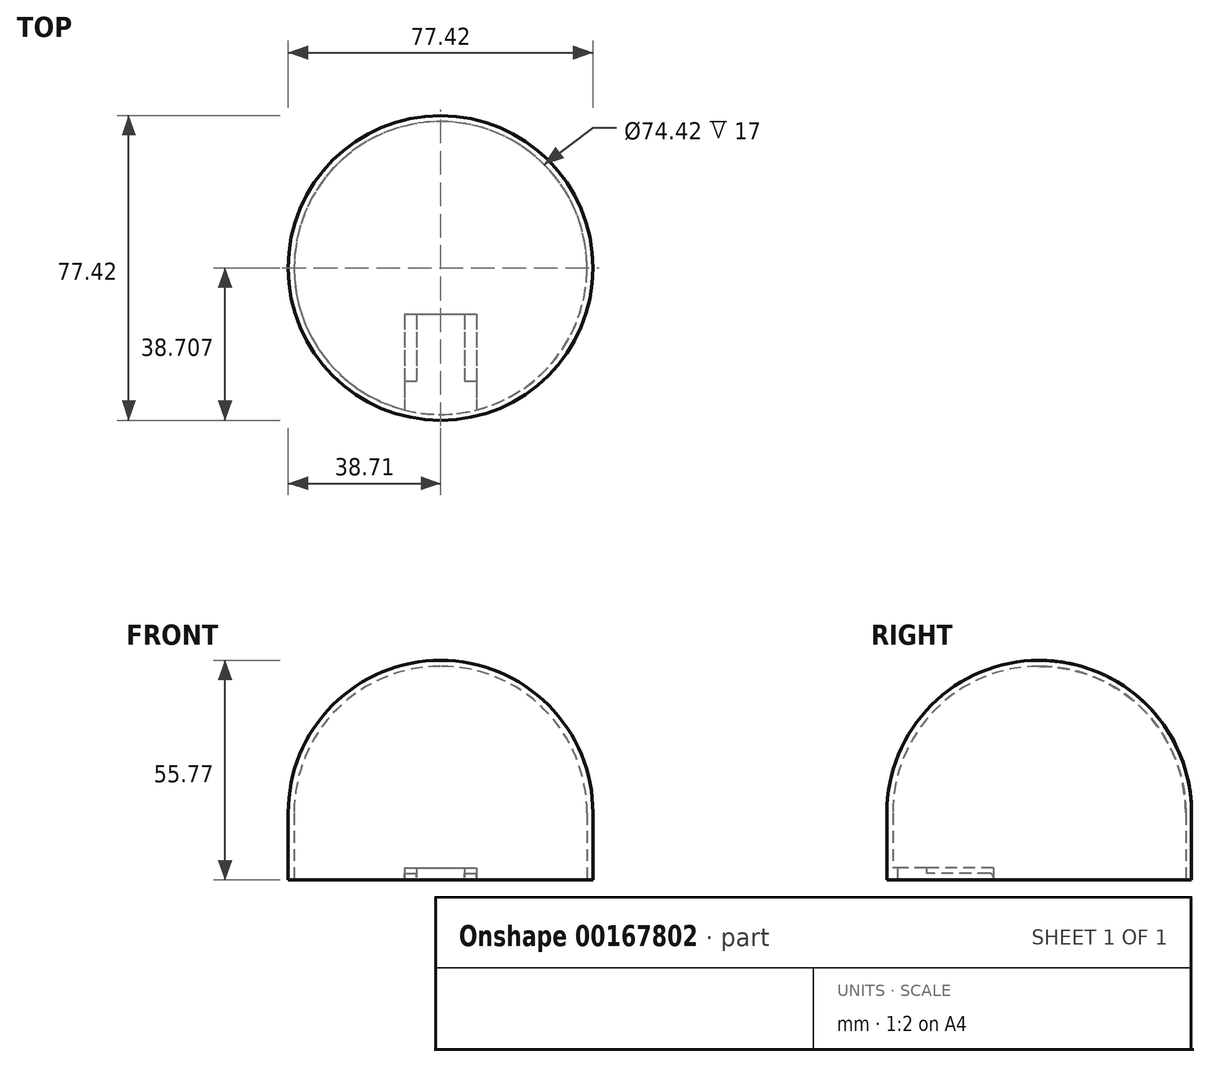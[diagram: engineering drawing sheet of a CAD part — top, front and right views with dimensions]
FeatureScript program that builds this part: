
annotation { "Feature Type Name" : "Feature", "Feature Type Description" : "" }
export const myFeature = defineFeature(function(context is Context, id is Id, definition is map)
    precondition{}
    {
        {
            var Q0;
            Q0=qCreatedBy(makeId("Top.planeOp"),FACE);
            var sketch = newSketch(context, id + "F0", { "sketchPlane" : qUnion([Q0])});
            skLineSegment(sketch, "E0.bottom", {"start": v(-9.1, 8.5) * mm, "end": v(9.1, 8.5) * mm});
            skLineSegment(sketch, "E0.top", {"start": v(-9.1, -8.5) * mm, "end": v(9.1, -8.5) * mm});
            skLineSegment(sketch, "E0.left", {"start": v(-9.1, 8.5) * mm, "end": v(-9.1, -8.5) * mm});
            skLineSegment(sketch, "E0.right", {"start": v(9.1, 8.5) * mm, "end": v(9.1, -8.5) * mm});
            skPoint(sketch, "E0.middle", {"position": v(0, 0) * mm});
            skLineSegment(sketch, "E1.bottom", {"start": v(-6.05, 8.5) * mm, "end": v(6.05, 8.5) * mm});
            skLineSegment(sketch, "E1.top", {"start": v(-6.05, -8.5) * mm, "end": v(6.05, -8.5) * mm});
            skLineSegment(sketch, "E1.left", {"start": v(-6.05, 8.5) * mm, "end": v(-6.05, -8.5) * mm});
            skLineSegment(sketch, "E1.right", {"start": v(6.05, 8.5) * mm, "end": v(6.05, -8.5) * mm});
            skLineSegment(sketch, "E2.top", {"start": v(-9.1, -16.5) * mm, "end": v(9.1, -16.5) * mm});
            skLineSegment(sketch, "E2.left", {"start": v(-9.1, -8.5) * mm, "end": v(-9.1, -16.5) * mm});
            skLineSegment(sketch, "E2.right", {"start": v(9.1, -8.5) * mm, "end": v(9.1, -16.5) * mm});
            skLineSegment(sketch, "E3", {"start": v(0, -8.5) * mm, "end": v(-26, -8.5) * mm});
            skLineSegment(sketch, "E4", {"start": v(0, -8.5) * mm, "end": v(26, -8.5) * mm});
            skLineSegment(sketch, "E5", {"start": v(0, -16.5) * mm, "end": v(0, 48.5) * mm});
            skCircle(sketch, "E6", {"center": v(0, 20.18) * mm, "radius": 38.7 * mm});
            skCircle(sketch, "E7", {"center": v(0, 20.18) * mm, "radius": 37.2 * mm});
            skSolve(sketch);
        }
        {
            var Q0;
            {var subQ0=sQuery(id+"F0.wireOp",EDGE,"E0.left");Q0=makeQuery(id+"F0.imprint","IMPRINT",FACE,{"disambiguationData":[TD([[makeQuery(id+"F0.imprint","IMPRINT",EDGE,{"derivedFrom":subQ0}),1.0]])]});}
            var Q1;
            {var subQ0=sQuery(id+"F0.wireOp",EDGE,"E0.right");Q1=makeQuery(id+"F0.imprint","IMPRINT",FACE,{"disambiguationData":[TD([[makeQuery(id+"F0.imprint","IMPRINT",EDGE,{"derivedFrom":subQ0}),-1.0]])]});}
            extrude(context, id + "F1", {"entities" : qUnion([Q0, Q1]), "depth" : 1.7 * mm});
        }
        {
            var Q0;
            {var subQ0=sQuery(id+"F0.wireOp",EDGE,"E1.left");Q0=makeQuery(id+"F0.imprint","IMPRINT",FACE,{"disambiguationData":[TD([[makeQuery(id+"F0.imprint","IMPRINT",EDGE,{"derivedFrom":subQ0}),1.0]])]});}
            var Q1;
            {var subQ0=sQuery(id+"F0.wireOp",EDGE,"E1.right");Q1=makeQuery(id+"F0.imprint","IMPRINT",FACE,{"disambiguationData":[TD([[makeQuery(id+"F0.imprint","IMPRINT",EDGE,{"derivedFrom":subQ0}),-1.0]])]});}
            var Q2;
            {var subQ4=sQuery(id+"F0.wireOp",EDGE,"E5");var subQ6=sQuery(id+"F0.wireOp",EDGE,"E2.top");var subQ7=makeQuery(id+"F0.imprint","INTERSECT",VERTEX,{"derivedFrom":[subQ6,subQ4]});Q2=makeQuery(id+"F0.imprint","IMPRINT",FACE,{"disambiguationData":[TD([[makeQuery(id+"F0.imprint","IMPRINT",EDGE,{"disambiguationData":[TD([[subQ7,1.0]])],"derivedFrom":subQ6}),1.0]])]});}
            var Q3;
            {var subQ4=sQuery(id+"F0.wireOp",EDGE,"E5");var subQ8=sQuery(id+"F0.wireOp",EDGE,"E2.top");var subQ9=makeQuery(id+"F0.imprint","INTERSECT",VERTEX,{"derivedFrom":[subQ8,subQ4]});Q3=makeQuery(id+"F0.imprint","IMPRINT",FACE,{"disambiguationData":[TD([[makeQuery(id+"F0.imprint","IMPRINT",EDGE,{"disambiguationData":[TD([[subQ9,-1.0]])],"derivedFrom":subQ8}),1.0]])]});}
            var Q4;
            {var subQ0=sQuery(id+"F0.wireOp",EDGE,"E2.top");var subQ1=makeQuery(id+"F0.imprint","INTERSECT",VERTEX,{"derivedFrom":[subQ0,sQuery(id+"F0.wireOp",EDGE,"E5")]});Q4=makeQuery(id+"F0.imprint","IMPRINT",FACE,{"disambiguationData":[TD([[makeQuery(id+"F0.imprint","IMPRINT",EDGE,{"disambiguationData":[TD([[subQ1,1.0]])],"derivedFrom":subQ0}),-1.0]])]});}
            var Q5;
            {var subQ0=sQuery(id+"F0.wireOp",EDGE,"E2.left");var subQ1=sQuery(id+"F0.wireOp",EDGE,"E2.top");var subQ2=makeQuery(id+"F0.imprint","INTERSECT",VERTEX,{"derivedFrom":[subQ1,subQ0]});Q5=makeQuery(id+"F0.imprint","IMPRINT",FACE,{"disambiguationData":[TD([[makeQuery(id+"F0.imprint","IMPRINT",EDGE,{"disambiguationData":[TD([[subQ2,-1.0]])],"derivedFrom":subQ1}),1.0]])]});}
            var Q6;
            {var subQ0=sQuery(id+"F0.wireOp",EDGE,"E2.right");var subQ1=sQuery(id+"F0.wireOp",EDGE,"E2.top");var subQ2=makeQuery(id+"F0.imprint","INTERSECT",VERTEX,{"derivedFrom":[subQ1,subQ0]});Q6=makeQuery(id+"F0.imprint","IMPRINT",FACE,{"disambiguationData":[TD([[makeQuery(id+"F0.imprint","IMPRINT",EDGE,{"disambiguationData":[TD([[subQ2,1.0]])],"derivedFrom":subQ1}),1.0]])]});}
            extrude(context, id + "F2", {"entities" : qUnion([Q0, Q1, Q2, Q3, Q4, Q5, Q6]), "operationType" : NewBodyOperationType.ADD, "depth" : 3 * mm});
        }
        {
            var Q0;
            {var subQ0=sQuery(id+"F0.wireOp",EDGE,"E2.left");var subQ1=sQuery(id+"F0.wireOp",EDGE,"E2.top");var subQ2=makeQuery(id+"F0.imprint","INTERSECT",VERTEX,{"derivedFrom":[subQ1,subQ0]});Q0=makeQuery(id+"F0.imprint","IMPRINT",FACE,{"disambiguationData":[TD([[makeQuery(id+"F0.imprint","IMPRINT",EDGE,{"disambiguationData":[TD([[subQ2,-1.0]])],"derivedFrom":subQ1}),1.0]])]});}
            var Q1;
            {var subQ1=sQuery(id+"F0.wireOp",EDGE,"E2.top");var subQ10=sQuery(id+"F0.wireOp",EDGE,"E2.left");var subQ11=makeQuery(id+"F0.imprint","INTERSECT",VERTEX,{"derivedFrom":[subQ1,subQ10]});Q1=makeQuery(id+"F0.imprint","IMPRINT",FACE,{"disambiguationData":[TD([[makeQuery(id+"F0.imprint","IMPRINT",EDGE,{"disambiguationData":[TD([[subQ11,-1.0]])],"derivedFrom":subQ1}),-1.0]])]});}
            var Q2;
            {var subQ0=sQuery(id+"F0.wireOp",EDGE,"E2.right");var subQ1=sQuery(id+"F0.wireOp",EDGE,"E2.top");var subQ2=makeQuery(id+"F0.imprint","INTERSECT",VERTEX,{"derivedFrom":[subQ1,subQ0]});Q2=makeQuery(id+"F0.imprint","IMPRINT",FACE,{"disambiguationData":[TD([[makeQuery(id+"F0.imprint","IMPRINT",EDGE,{"disambiguationData":[TD([[subQ2,1.0]])],"derivedFrom":subQ1}),1.0]])]});}
            var Q3;
            {var subQ0=sQuery(id+"F0.wireOp",EDGE,"E6");var subQ1=sQuery(id+"F0.wireOp",EDGE,"E3");var subQ2=makeQuery(id+"F0.imprint","INTERSECT",VERTEX,{"derivedFrom":[subQ1,subQ0]});Q3=makeQuery(id+"F0.imprint","IMPRINT",FACE,{"disambiguationData":[TD([[makeQuery(id+"F0.imprint","IMPRINT",EDGE,{"disambiguationData":[TD([[subQ2,1.0]])],"derivedFrom":subQ1}),-1.0]])]});}
            extrude(context, id + "F3", {"entities" : qUnion([Q0, Q1, Q2, Q3]), "operationType" : NewBodyOperationType.ADD, "depth" : 17 * mm});
        }
        {
            var Q0;
            {var subQ0=sQuery(id+"F0.wireOp",EDGE,"E0.bottom");Q0=makeQuery(id+"F1.opExtrude","CAP_EDGE",EDGE,{"disambiguationData":[OSD([subQ0]),TDD([makeQuery(id+"F0.imprint","IMPRINT",EDGE,{"disambiguationData":[TD([[makeQuery(id+"F0.imprint","INTERSECT",VERTEX,{"derivedFrom":[subQ0,sQuery(id+"F0.wireOp",EDGE,"E0.right")]}),1.0]])],"derivedFrom":subQ0})])],"isStart":false});}
            var Q1;
            {var subQ0=sQuery(id+"F0.wireOp",EDGE,"E0.bottom");Q1=makeQuery(id+"F1.opExtrude","CAP_EDGE",EDGE,{"disambiguationData":[OSD([subQ0]),TDD([makeQuery(id+"F0.imprint","IMPRINT",EDGE,{"disambiguationData":[TD([[makeQuery(id+"F0.imprint","INTERSECT",VERTEX,{"derivedFrom":[subQ0,sQuery(id+"F0.wireOp",EDGE,"E0.left")]}),-1.0]])],"derivedFrom":subQ0})])],"isStart":false});}
            var Q2;
            Q2=makeQuery(id+"F2.opExtrude","CAP_EDGE",EDGE,{"disambiguationData":[OSD([sQuery(id+"F0.wireOp",EDGE,"E1.bottom")])],"isStart":false});
            fillet(context, id + "F4", {"entities" : qUnion([Q0, Q1, Q2]), "radius" : 1 * mm, "tangentPropagation" : true, "allowEdgeOverflow" : false});
        }
        {
            var Q0;
            Q0=qCreatedBy(makeId("Right.planeOp"),FACE);
            var sketch = newSketch(context, id + "F5", { "sketchPlane" : qUnion([Q0])});
            skLineSegment(sketch, "E8.0", {"start": v(-18.53, 0) * mm, "end": v(58.89, 0) * mm});
            skLineSegment(sketch, "E9", {"start": v(20.18, 0) * mm, "end": v(20.18, 60.35) * mm});
            skLineSegment(sketch, "E10", {"start": v(58.89, 0) * mm, "end": v(58.89, 17) * mm});
            skCircle(sketch, "E11", {"center": v(20.18, 17.06) * mm, "radius": 38.7 * mm});
            skCircle(sketch, "E12", {"center": v(20.18, 17.06) * mm, "radius": 37.2 * mm});
            skLineSegment(sketch, "E13", {"start": v(58.89, 17) * mm, "end": v(20.18, 17.06) * mm});
            skSolve(sketch);
        }
        {
            var Q0;
            {var subQ0=sQuery(id+"F5.wireOp",EDGE,"E11");var subQ1=sQuery(id+"F5.wireOp",EDGE,"E9");var subQ2=makeQuery(id+"F5.imprint","INTERSECT",VERTEX,{"derivedFrom":[subQ1,subQ0]});Q0=makeQuery(id+"F5.imprint","IMPRINT",FACE,{"disambiguationData":[TD([[makeQuery(id+"F5.imprint","IMPRINT",EDGE,{"disambiguationData":[TD([[subQ2,1.0]])],"derivedFrom":subQ1}),-1.0]])]});}
            var Q1;
            Q1=sQuery(id+"F5.wireOp",EDGE,"E9");
            revolve(context, id + "F6", {"operationType" : NewBodyOperationType.ADD, "entities" : qUnion([Q0]), "axis" : qUnion([Q1]), "revolveType" : RevolveType.FULL});
        }
    });
